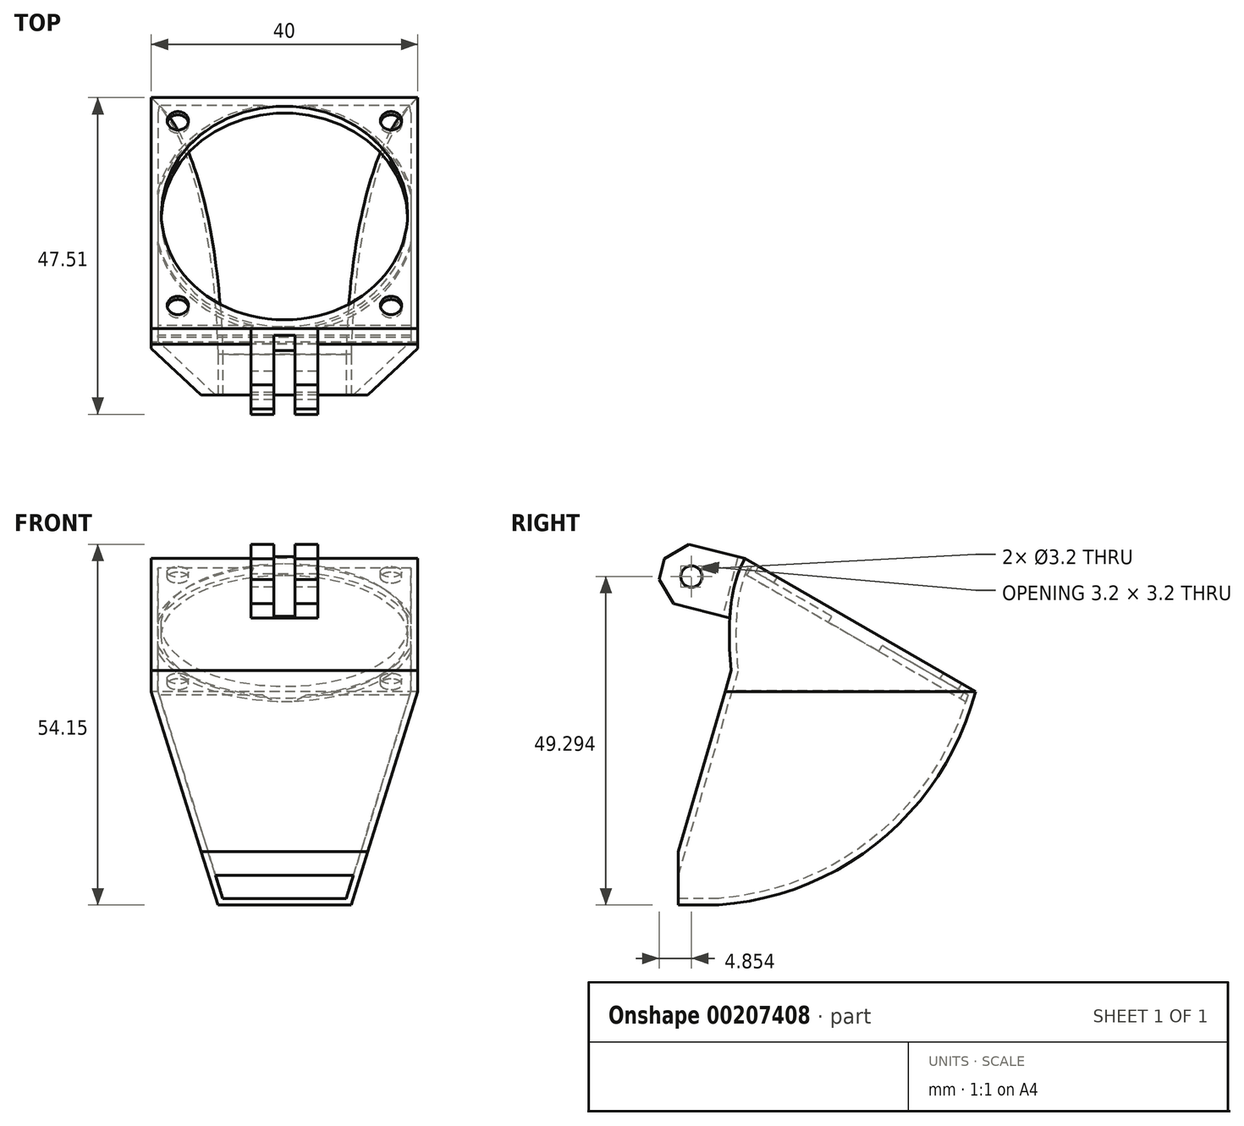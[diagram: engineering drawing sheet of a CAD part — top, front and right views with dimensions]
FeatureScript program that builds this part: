
annotation { "Feature Type Name" : "Feature", "Feature Type Description" : "" }
export const myFeature = defineFeature(function(context is Context, id is Id, definition is map)
    precondition{}
    {
        {
            var Q0;
            Q0=qCreatedBy(makeId("Right.planeOp"),FACE);
            var sketch = newSketch(context, id + "F0", { "sketchPlane" : qUnion([Q0])});
            skLineSegment(sketch, "E0", {"start": v(0, 8) * mm, "end": v(0, 0) * mm});
            skLineSegment(sketch, "E1", {"start": v(44.64, 32) * mm, "end": v(10, 52) * mm});
            skFitSpline(sketch, "E2", {"points": [v(10, 52) * mm, v(0, 8) * mm], "startDerivative": vector(-30, -55.3) * mm, "endDerivative": vector(-80.88, 56) * mm});
            skPoint(sketch, "E3", {"position": v(7.96, 35.2) * mm});
            skLineSegment(sketch, "E4", {"start": v(7.96, 35.2) * mm, "end": v(0, 8) * mm});
            skPoint(sketch, "E5", {"position": v(37.42, 0) * mm});
            skPoint(sketch, "E6", {"position": v(37.42, 9.3) * mm});
            skArc(sketch, "E7", {"start": v(0, 0) * mm, "mid": v(28.1, 7.94) * mm, "end": v(44.64, 32) * mm});
            skSolve(sketch);
        }
        {
            var Q0;
            Q0=qSketchRegion(id+"F0",true);
            extrude(context, id + "F1", {"entities" : qUnion([Q0]), "depth" : 40 * mm, "symmetric" : true});
        }
        {
            var Q0;
            Q0=qCreatedBy(makeId("Front.planeOp"),FACE);
            var sketch = newSketch(context, id + "F2", { "sketchPlane" : qUnion([Q0])});
            skLineSegment(sketch, "E8", {"start": v(10, 0) * mm, "end": v(-10, 0) * mm});
            skLineSegment(sketch, "E9", {"start": v(20, 52) * mm, "end": v(-20, 52) * mm});
            skLineSegment(sketch, "E10", {"start": v(-20, 52) * mm, "end": v(-20, 32) * mm});
            skLineSegment(sketch, "E11", {"start": v(20, 52) * mm, "end": v(20, 32) * mm});
            skPoint(sketch, "E12", {"position": v(0, 0) * mm});
            skLineSegment(sketch, "E13", {"start": v(-20, 32) * mm, "end": v(-10, 0) * mm});
            skLineSegment(sketch, "E14", {"start": v(20, 32) * mm, "end": v(10, 0) * mm});
            skSolve(sketch);
        }
        {
            var Q0;
            Q0=qSketchRegion(id+"F2",true);
            var Q1;
            Q1=makeQuery(id+"F1.opExtrude","SWEPT_BODY",BODY,{"disambiguationData":[OSD([sQuery(id+"F0.wireOp",EDGE,"E0"),sQuery(id+"F0.wireOp",EDGE,"E1"),sQuery(id+"F0.wireOp",EDGE,"E2"),sQuery(id+"F0.wireOp",EDGE,"E4"),sQuery(id+"F0.wireOp",EDGE,"E7")])]});
            extrude(context, id + "F3", {"entities" : qUnion([Q0]), "operationType" : NewBodyOperationType.INTERSECT, "endBound" : BoundingType.UP_TO_BODY, "oppositeDirection" : true, "endBoundEntityBody" : qUnion([Q1]), "depth" : 25 * mm});
        }
        {
            var Q0;
            Q0=makeQuery(id+"F1.opExtrude","SWEPT_FACE",FACE,{"disambiguationData":[OSD([sQuery(id+"F0.wireOp",EDGE,"E1")])]});
            var sketch = newSketch(context, id + "F4", { "sketchPlane" : qUnion([Q0])});
            skLineSegment(sketch, "E15", {"start": v(20, -17.34) * mm, "end": v(-20, 22.66) * mm, "construction": true});
            skLineSegment(sketch, "E16", {"start": v(-20, -17.34) * mm, "end": v(20, 22.66) * mm, "construction": true});
            skCircle(sketch, "E17", {"center": v(0, 2.66) * mm, "radius": 18.5 * mm});
            skSolve(sketch);
        }
        {
            var Q0;
            Q0=qSketchRegion(id+"F4",true);
            extrude(context, id + "F5", {"entities" : qUnion([Q0]), "operationType" : NewBodyOperationType.REMOVE, "oppositeDirection" : true, "depth" : 2 * mm});
        }
        {
            var Q0;
            Q0=makeQuery(id+"F5.boolean.opBoolean","COPY",FACE,{"derivedFrom":makeQuery(id+"F5.opExtrude","CAP_FACE",FACE,{"disambiguationData":[OSD([sQuery(id+"F4.wireOp",EDGE,"E17")])],"isStart":false})});
            var Q1;
            Q1=makeQuery(id+"F1.opExtrude","SWEPT_FACE",FACE,{"disambiguationData":[OSD([sQuery(id+"F0.wireOp",EDGE,"E0")])]});
            shell(context, id + "F6", {"entities" : qUnion([Q0, Q1]), "thickness" : 1 * mm});
        }
        {
            var Q0;
            Q0=makeQuery(id+"F1.opExtrude","SWEPT_FACE",FACE,{"disambiguationData":[OSD([sQuery(id+"F0.wireOp",EDGE,"E1")])]});
            var sketch = newSketch(context, id + "F7", { "sketchPlane" : qUnion([Q0])});
            skCircle(sketch, "E18", {"center": v(16, 18.66) * mm, "radius": 1.6 * mm});
            skCircle(sketch, "E19", {"center": v(-16, 18.66) * mm, "radius": 1.6 * mm});
            skCircle(sketch, "E20", {"center": v(-16, -13.34) * mm, "radius": 1.6 * mm});
            skCircle(sketch, "E21", {"center": v(16, -13.34) * mm, "radius": 1.6 * mm});
            skPoint(sketch, "E22", {"position": v(-20, 2.66) * mm});
            skSolve(sketch);
        }
        {
            var Q0;
            Q0=qSketchRegion(id+"F7",true);
            var Q1;
            Q1=makeQuery(id+"F6.opShell","OFFSET_FACE",FACE,{"disambiguationData":[OSD([sQuery(id+"F0.wireOp",EDGE,"E1")]),OD(1.0)]});
            extrude(context, id + "F8", {"entities" : qUnion([Q0]), "operationType" : NewBodyOperationType.REMOVE, "endBound" : BoundingType.UP_TO_SURFACE, "oppositeDirection" : true, "endBoundEntityFace" : qUnion([Q1]), "depth" : 25 * mm});
        }
        {
            var Q0;
            Q0=qCreatedBy(makeId("Right.planeOp"),FACE);
            var sketch = newSketch(context, id + "F9", { "sketchPlane" : qUnion([Q0])});
            skLineSegment(sketch, "E23", {"start": v(-1.34, 54.89) * mm, "end": v(-3.6, 45.97) * mm});
            skLineSegment(sketch, "E24", {"start": v(-3.6, 45.97) * mm, "end": v(7.73, 43.08) * mm});
            skLineSegment(sketch, "E25", {"start": v(7.73, 43.08) * mm, "end": v(10, 52) * mm});
            skLineSegment(sketch, "E26", {"start": v(10, 52) * mm, "end": v(8.06, 52.5) * mm});
            skLineSegment(sketch, "E27", {"start": v(8.06, 52.5) * mm, "end": v(8.06, 52.5) * mm});
            skLineSegment(sketch, "E28", {"start": v(8.06, 52.5) * mm, "end": v(-1.34, 54.89) * mm});
            skCircle(sketch, "E29", {"center": v(1.98, 49.3) * mm, "radius": 1.6 * mm});
            skSolve(sketch);
        }
        {
            var Q0;
            Q0=qSketchRegion(id+"F9",true);
            extrude(context, id + "F10", {"entities" : qUnion([Q0]), "operationType" : NewBodyOperationType.ADD, "depth" : 10 * mm, "symmetric" : true});
        }
        {
            var Q0;
            {var subQ0=sQuery(id+"F9.wireOp",EDGE,"E24");Q0=makeQuery(id+"F10.boolean.opBoolean","SPLIT",FACE,{"disambiguationData":[TD([makeQuery(id+"F1.opExtrude","SWEPT_FACE",FACE,{"disambiguationData":[OSD([sQuery(id+"F0.wireOp",EDGE,"E2")])]})])],"derivedFrom":makeQuery(id+"F10.opExtrude","SWEPT_FACE",FACE,{"disambiguationData":[OSD([subQ0])]})});}
            var sketch = newSketch(context, id + "F11", { "sketchPlane" : qUnion([Q0])});
            skLineSegment(sketch, "E30.top", {"start": v(1.6, 4.23) * mm, "end": v(-1.6, 4.23) * mm});
            skLineSegment(sketch, "E30.left", {"start": v(1.6, 14.84) * mm, "end": v(1.6, 4.23) * mm});
            skLineSegment(sketch, "E30.right", {"start": v(-1.6, 14.84) * mm, "end": v(-1.6, 4.23) * mm});
            skPoint(sketch, "E31", {"position": v(0, 13.63) * mm});
            skSolve(sketch);
        }
        {
            var Q0;
            {var subQ0=sQuery(id+"F11.wireOp",EDGE,"E30.left");var subQ1=sQuery(id+"F9.wireOp",EDGE,"E24");var subQ2=makeQuery(id+"F10.opExtrude","SWEPT_EDGE",EDGE,{"disambiguationData":[OSD([sQuery(id+"F9.wireOp",EDGE,"E23"),subQ1])]});var subQ3=makeQuery(id+"F11.imprint","INTERSECT",VERTEX,{"derivedFrom":[subQ2,subQ0]});Q0=makeQuery(id+"F11.imprint","IMPRINT",FACE,{"disambiguationData":[TD([[makeQuery(id+"F11.imprint","IMPRINT",EDGE,{"disambiguationData":[TD([[subQ3,-1.0]])],"derivedFrom":subQ0}),-1.0]])]});}
            var Q1;
            Q1=makeQuery(id+"F10.boolean.opBoolean","MERGE",FACE,{"derivedFrom":[makeQuery(id+"F1.opExtrude","SWEPT_FACE",FACE,{"disambiguationData":[OSD([sQuery(id+"F0.wireOp",EDGE,"E1")])]}),makeQuery(id+"F10.opExtrude","SWEPT_FACE",FACE,{"disambiguationData":[OSD([sQuery(id+"F9.wireOp",EDGE,"E26"),sQuery(id+"F9.wireOp",EDGE,"E28")])]})]});
            extrude(context, id + "F12", {"entities" : qUnion([Q0]), "operationType" : NewBodyOperationType.REMOVE, "endBound" : BoundingType.UP_TO_SURFACE, "oppositeDirection" : true, "endBoundEntityFace" : qUnion([Q1]), "depth" : 25 * mm});
        }
        {
            var Q0;
            {var subQ0=sQuery(id+"F9.wireOp",EDGE,"E23");var subQ1=sQuery(id+"F9.wireOp",EDGE,"E24");Q0=makeQuery(id+"F12.boolean.opBoolean","SPLIT",EDGE,{"disambiguationData":[TD([makeQuery(id+"F12.opExtrude","SWEPT_FACE",FACE,{"disambiguationData":[OSD([sQuery(id+"F11.wireOp",EDGE,"E30.right")])]})])],"derivedFrom":makeQuery(id+"F10.opExtrude","SWEPT_EDGE",EDGE,{"disambiguationData":[OSD([subQ0,subQ1])]})});}
            var Q1;
            {var subQ0=sQuery(id+"F9.wireOp",EDGE,"E23");var subQ1=sQuery(id+"F9.wireOp",EDGE,"E24");Q1=makeQuery(id+"F12.boolean.opBoolean","SPLIT",EDGE,{"disambiguationData":[TD([makeQuery(id+"F12.opExtrude","SWEPT_FACE",FACE,{"disambiguationData":[OSD([sQuery(id+"F11.wireOp",EDGE,"E30.left")])]})])],"derivedFrom":makeQuery(id+"F10.opExtrude","SWEPT_EDGE",EDGE,{"disambiguationData":[OSD([subQ0,subQ1])]})});}
            var Q2;
            {var subQ0=sQuery(id+"F9.wireOp",EDGE,"E28");var subQ2=sQuery(id+"F9.wireOp",EDGE,"E23");Q2=makeQuery(id+"F12.boolean.opBoolean","SPLIT",EDGE,{"disambiguationData":[TD([makeQuery(id+"F12.opExtrude","SWEPT_FACE",FACE,{"disambiguationData":[OSD([sQuery(id+"F11.wireOp",EDGE,"E30.right")])]})])],"derivedFrom":makeQuery(id+"F10.opExtrude","SWEPT_EDGE",EDGE,{"disambiguationData":[OSD([subQ2,subQ0])]})});}
            var Q3;
            {var subQ0=sQuery(id+"F9.wireOp",EDGE,"E28");var subQ2=sQuery(id+"F9.wireOp",EDGE,"E23");Q3=makeQuery(id+"F12.boolean.opBoolean","SPLIT",EDGE,{"disambiguationData":[TD([makeQuery(id+"F12.opExtrude","SWEPT_FACE",FACE,{"disambiguationData":[OSD([sQuery(id+"F11.wireOp",EDGE,"E30.left")])]})])],"derivedFrom":makeQuery(id+"F10.opExtrude","SWEPT_EDGE",EDGE,{"disambiguationData":[OSD([subQ2,subQ0])]})});}
            chamfer(context, id + "F13", {"entities" : qUnion([Q0, Q1, Q2, Q3]), "width" : 3 * mm, "tangentPropagation" : true});
        }
    });
